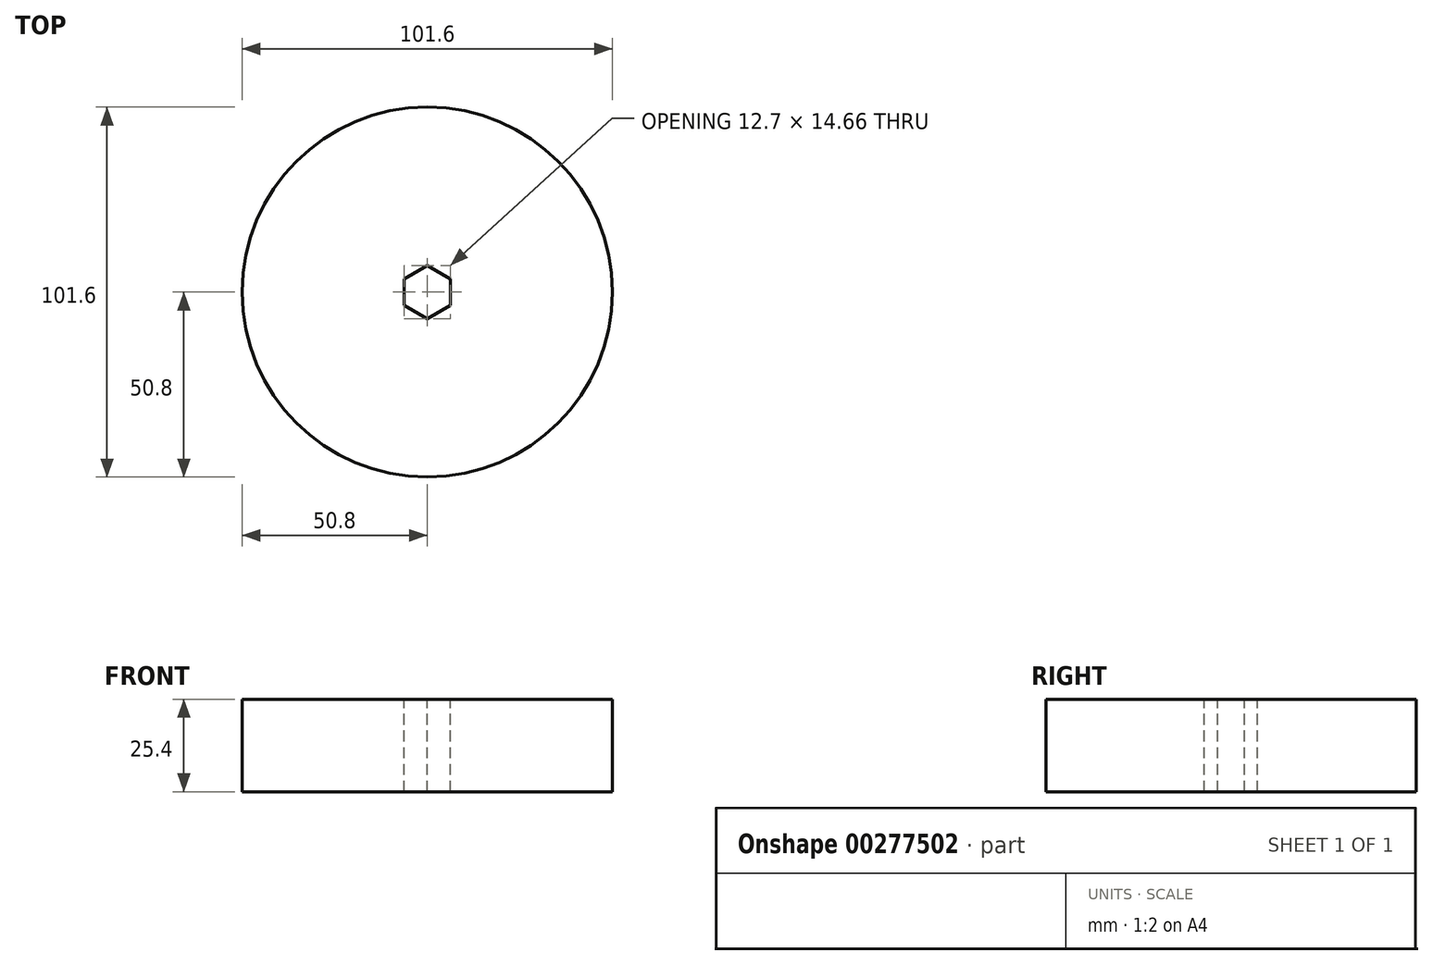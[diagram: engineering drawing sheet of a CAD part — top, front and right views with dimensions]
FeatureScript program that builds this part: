
annotation { "Feature Type Name" : "Feature", "Feature Type Description" : "" }
export const myFeature = defineFeature(function(context is Context, id is Id, definition is map)
    precondition{}
    {
        {
            var Q0;
            Q0=qCreatedBy(makeId("Top.planeOp"),FACE);
            var sketch = newSketch(context, id + "F0", { "sketchPlane" : qUnion([Q0])});
            skCircle(sketch, "E0", {"center": v(0, 0) * mm, "radius": 50.8 * mm});
            skSolve(sketch);
        }
        {
            var Q0;
            Q0 = qSketchRegion(id + "F0", true);
            extrude(context, id + "F1", {"entities" : qUnion([Q0]), "depth" : 25.4 * mm});
        }
        {
            var Q0;
            Q0=makeQuery(id+"F1.opExtrude","CAP_FACE",FACE,{"disambiguationData":[OSD([sQuery(id+"F0.wireOp",EDGE,"E0")])],"isStart":false});
            var sketch = newSketch(context, id + "F2", { "sketchPlane" : qUnion([Q0])});
            skCircle(sketch, "E1.cCircle", {"center": v(0, 0) * mm, "radius": 6.35 * mm, "construction": true});
            skLineSegment(sketch, "E1.0", {"start": v(6.35, 3.67) * mm, "end": v(6.35, -3.67) * mm});
            skLineSegment(sketch, "E1.1", {"start": v(6.35, -3.67) * mm, "end": v(0, -7.33) * mm});
            skLineSegment(sketch, "E1.2", {"start": v(0, -7.33) * mm, "end": v(-6.35, -3.67) * mm});
            skLineSegment(sketch, "E1.3", {"start": v(-6.35, -3.67) * mm, "end": v(-6.35, 3.67) * mm});
            skLineSegment(sketch, "E1.4", {"start": v(-6.35, 3.67) * mm, "end": v(0, 7.33) * mm});
            skLineSegment(sketch, "E1.5", {"start": v(0, 7.33) * mm, "end": v(6.35, 3.67) * mm});
            skPoint(sketch, "E1.0.midPoint", {"position": v(6.35, 0) * mm});
            skSolve(sketch);
        }
        {
            var Q0;
            Q0=makeQuery(id+"F2.imprint","IMPRINT",FACE,{"disambiguationData":[TD([[makeQuery(id+"F2.imprint","IMPRINT",EDGE,{"derivedFrom":sQuery(id+"F2.wireOp",EDGE,"E1.0")}),-1.0]])]});
            extrude(context, id + "F3", {"entities" : qUnion([Q0]), "operationType" : NewBodyOperationType.REMOVE, "oppositeDirection" : true, "depth" : 25.4 * mm});
        }
    });
